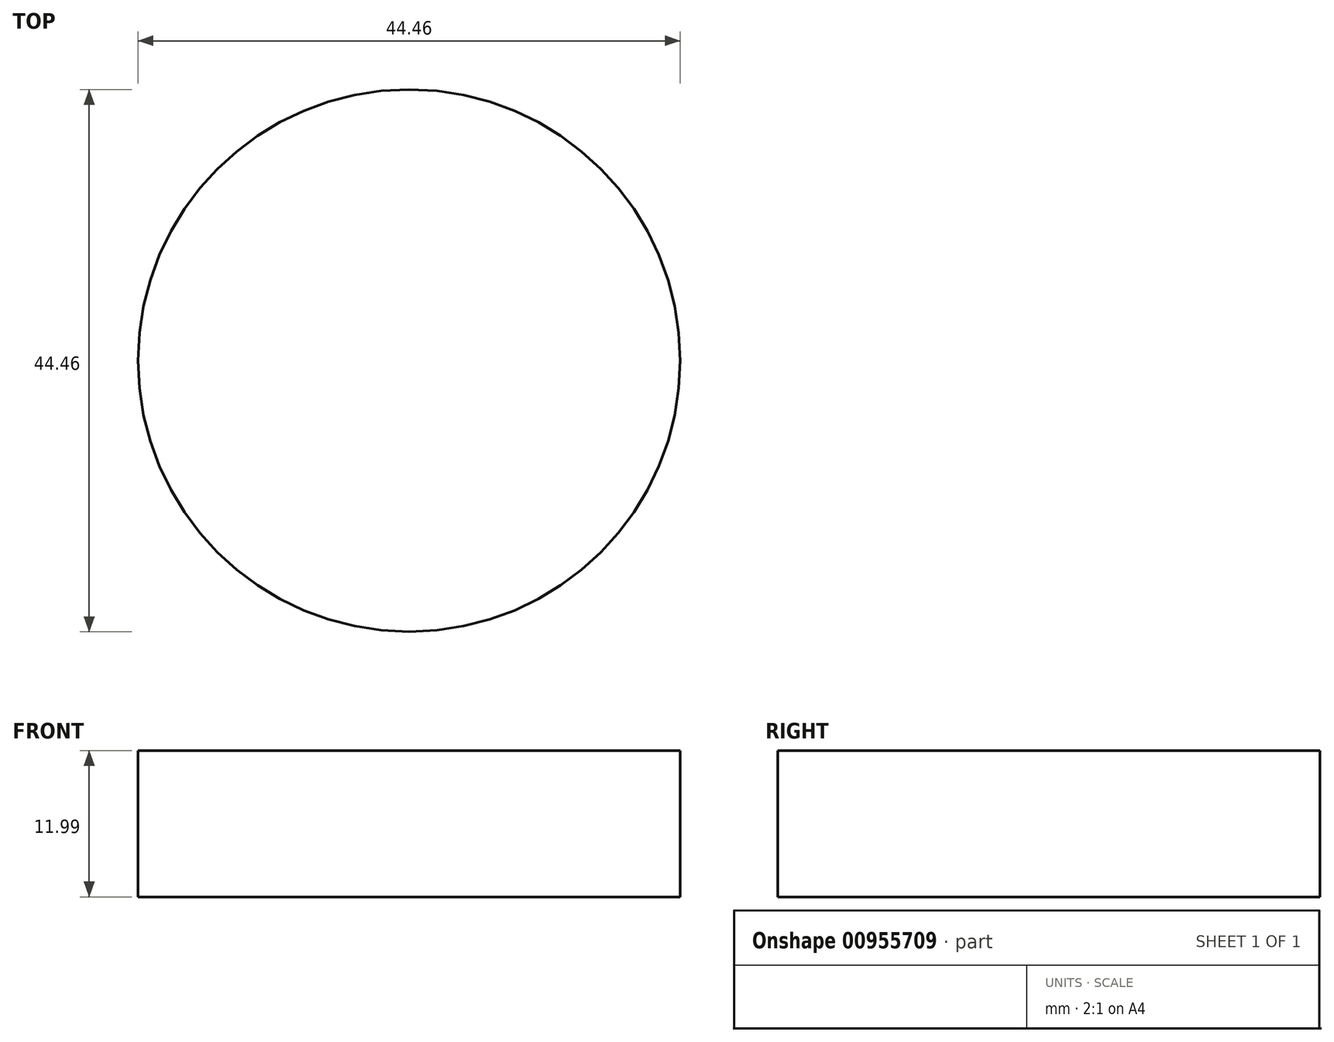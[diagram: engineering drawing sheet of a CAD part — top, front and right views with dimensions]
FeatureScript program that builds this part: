
annotation { "Feature Type Name" : "Feature", "Feature Type Description" : "" }
export const myFeature = defineFeature(function(context is Context, id is Id, definition is map)
    precondition{}
    {
        {
            var Q0;
            Q0=qCreatedBy(makeId("Top.planeOp"),FACE);
            var sketch = newSketch(context, id + "F0", { "sketchPlane" : qUnion([Q0])});
            skCircle(sketch, "E0", {"center": v(0, 0) * mm, "radius": 22.23 * mm});
            skSolve(sketch);
        }
        {
            var Q0;
            Q0 = qSketchRegion(id + "F0", true);
            extrude(context, id + "F1", {"entities" : qUnion([Q0]), "depth" : 12 * mm, "offsetDistance" : 25.4 * mm});
        }
    });
